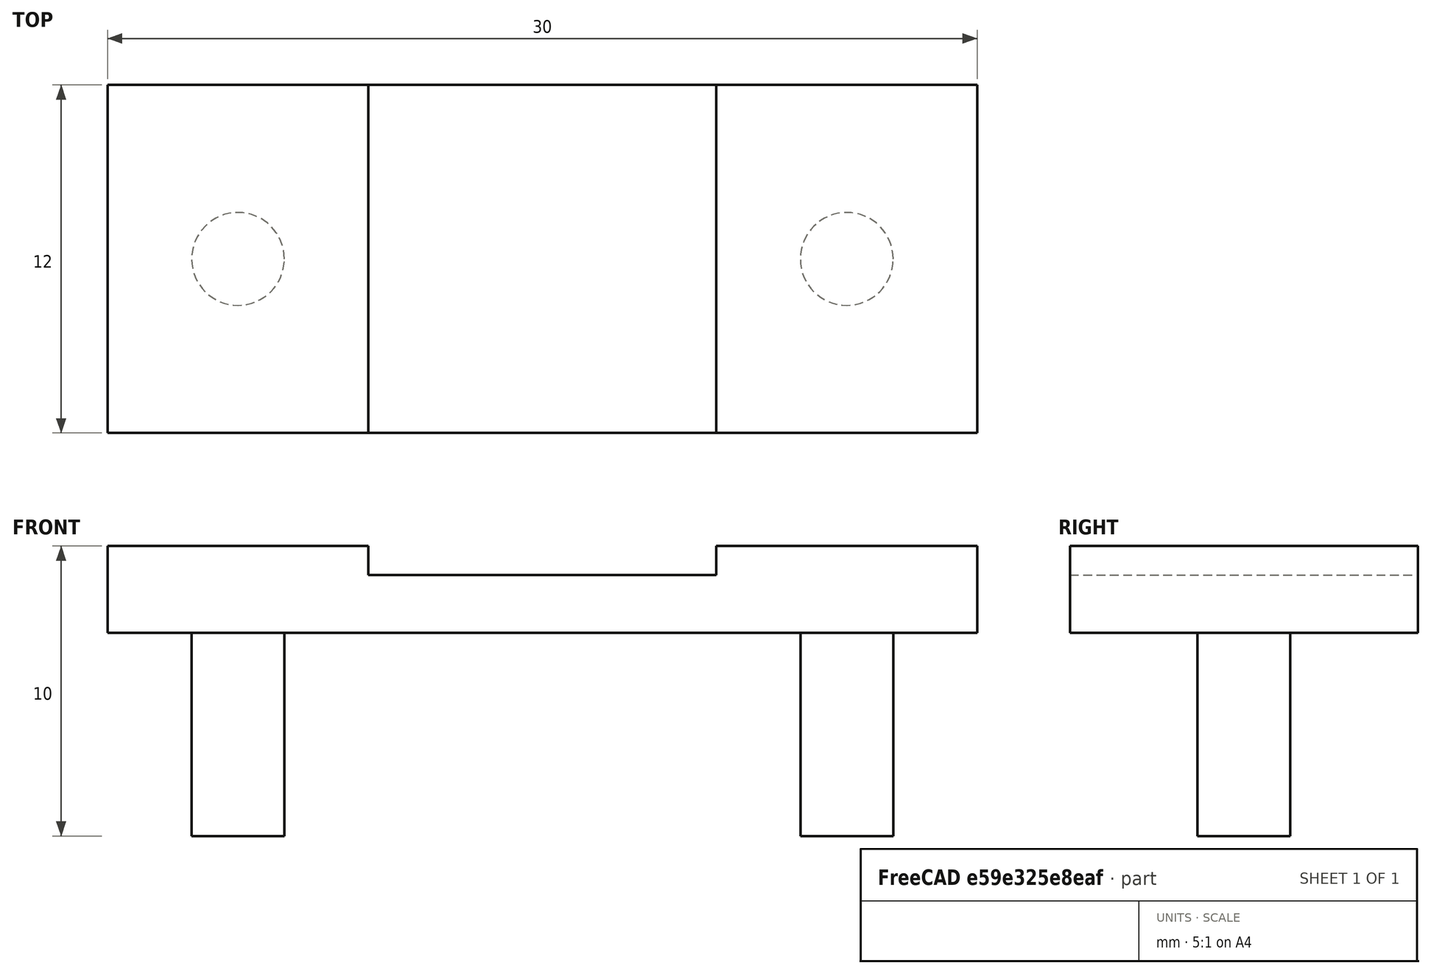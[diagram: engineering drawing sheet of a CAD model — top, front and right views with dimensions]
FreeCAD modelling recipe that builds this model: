
FCSTD DOCUMENT  (FreeCAD 0.17R13522 (Git))
Label: perforador_botones
License: CreativeCommons Attribution-ShareAlike
LicenseURL: http://creativecommons.org/licenses/by-sa/4.0/
objects: Part::Box×2, Part::Cylinder×2, Part::Fuse×2, Part::Cut×1
note: 7 computed .brp shape members not serialized (recipe doc carries the construction recipe); baked Part::Feature solids carry a one-line shape summary decoded from their .brp

FEATURE [Part::Box] Box  label="base"
  AttacherType = Attacher::AttachEngine3D
  Height = 3
  Length = 30
  Width = 12
FEATURE [Part::Box] Box001  label="posicion_para_boton"
  AttacherType = Attacher::AttachEngine3D
  Height = 1
  Length = 12
  Placement = pos=(9,0,2) rot=(0,0,1;0rad)
  Width = 12
FEATURE [Part::Cut] Cut
  Base = -> Box
  Refine = true
  Tool = -> Box001
FEATURE [Part::Cylinder] Cylinder
  Angle = 360
  AttacherType = Attacher::AttachEngine3D
  Height = 10
  Placement = pos=(25.5,6,-7) rot=(0,0,1;0rad)
  Radius = 1.6
FEATURE [Part::Cylinder] Cylinder001
  Angle = 360
  AttacherType = Attacher::AttachEngine3D
  Height = 10
  Placement = pos=(4.5,6,-7) rot=(0,0,1;0rad)
  Radius = 1.6
FEATURE [Part::Fuse] Fusion
  Base = -> Cut
  Refine = true
  Tool = -> Cylinder
FEATURE [Part::Fuse] Fusion001  label="el perforador boton"
  Base = -> Cylinder001
  Refine = true
  Tool = -> Fusion
